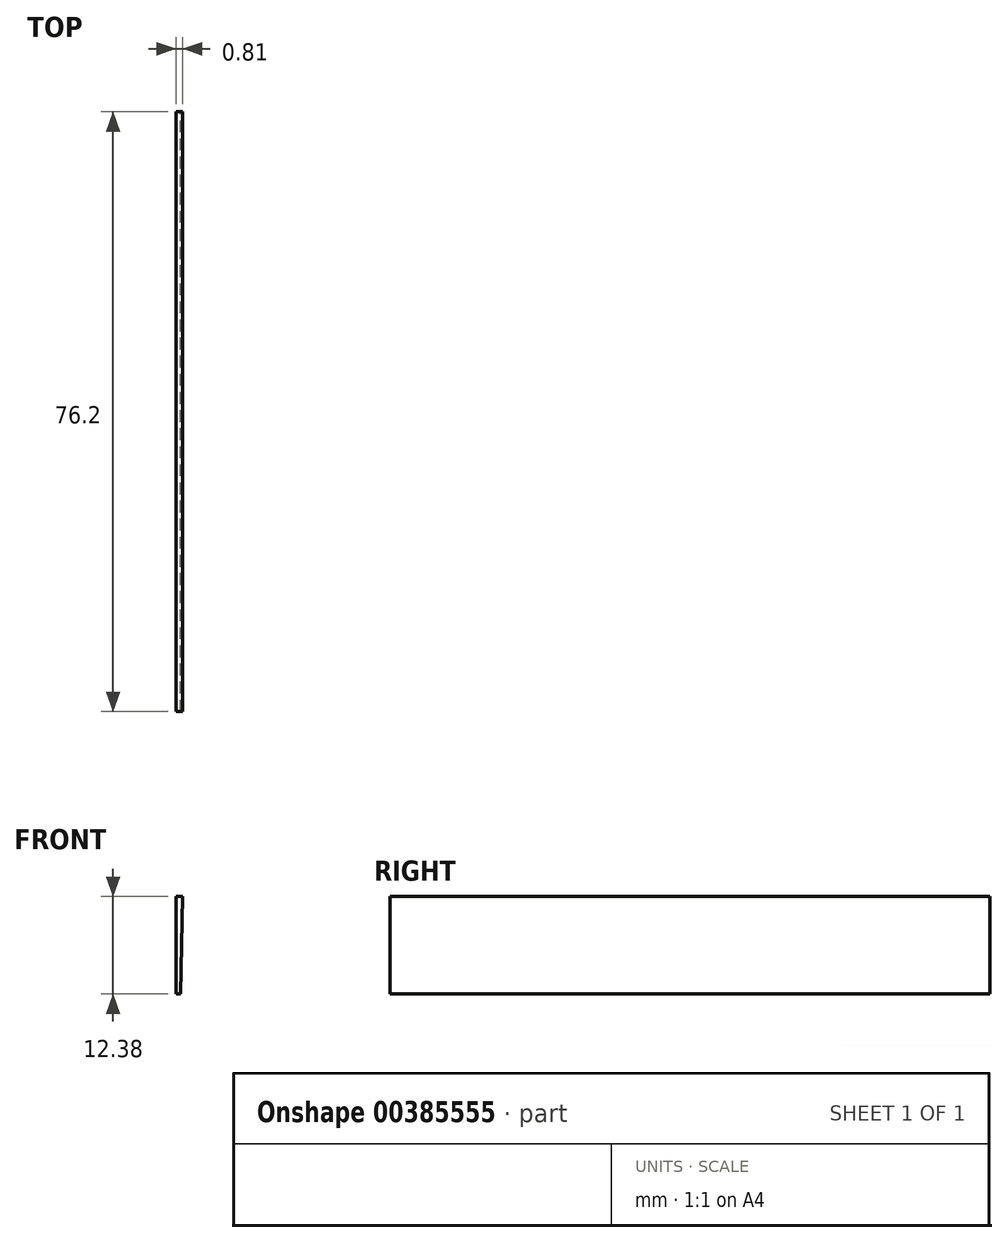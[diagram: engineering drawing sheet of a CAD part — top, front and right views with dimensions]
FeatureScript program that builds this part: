
annotation { "Feature Type Name" : "Feature", "Feature Type Description" : "" }
export const myFeature = defineFeature(function(context is Context, id is Id, definition is map)
    precondition{}
    {
        {
            var Q0;
            Q0=qCreatedBy(makeId("Right.planeOp"),FACE);
            var sketch = newSketch(context, id + "F0", { "sketchPlane" : qUnion([Q0])});
            skLineSegment(sketch, "E0.bottom", {"start": v(0, 46.35) * mm, "end": v(76.2, 46.35) * mm});
            skLineSegment(sketch, "E0.top", {"start": v(0, 33.97) * mm, "end": v(76.2, 33.97) * mm});
            skLineSegment(sketch, "E0.left", {"start": v(0, 46.35) * mm, "end": v(0, 33.97) * mm});
            skLineSegment(sketch, "E0.right", {"start": v(76.2, 46.35) * mm, "end": v(76.2, 33.97) * mm});
            skLineSegment(sketch, "E1", {"start": v(0, 0) * mm, "end": v(86.5, 0) * mm, "construction": true});
            skSolve(sketch);
        }
        {
            var Q0;
            Q0 = qSketchRegion(id + "F0", true);
            var Q1;
            Q1=sQuery(id+"F0.wireOp",EDGE,"E1");
            revolve(context, id + "F1", {"entities" : qUnion([Q0]), "axis" : qUnion([Q1]), "revolveType" : RevolveType.ONE_DIRECTION, "angle" : 1 * degree});
        }
    });
